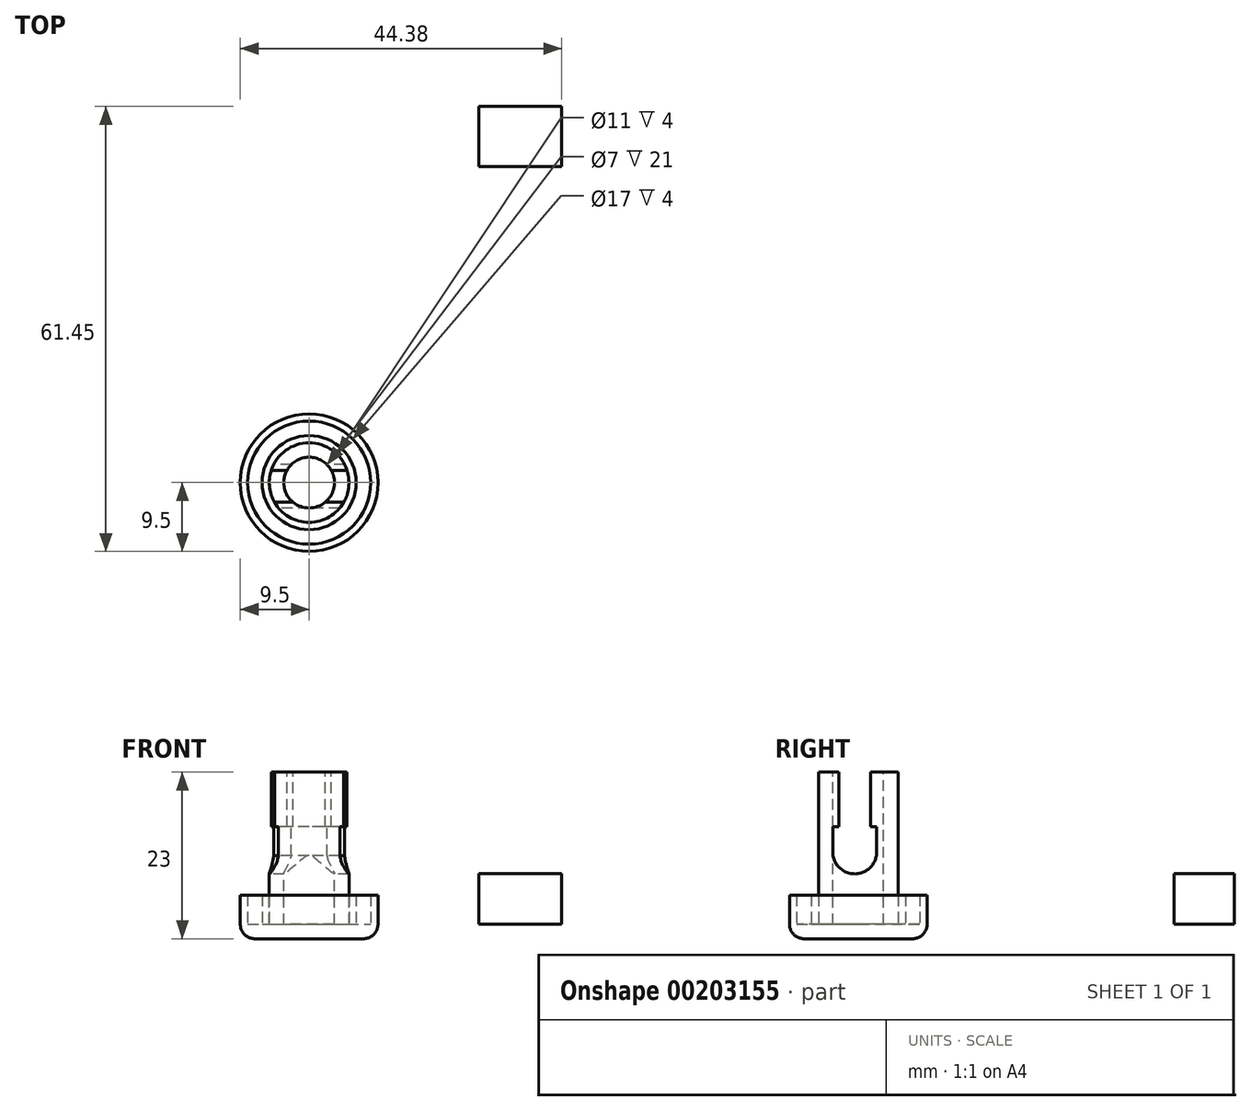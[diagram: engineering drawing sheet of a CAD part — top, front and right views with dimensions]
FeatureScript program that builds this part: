
annotation { "Feature Type Name" : "Feature", "Feature Type Description" : "" }
export const myFeature = defineFeature(function(context is Context, id is Id, definition is map)
    precondition{}
    {
        {
            var Q0;
            Q0=qCreatedBy(makeId("Top.planeOp"),FACE);
            var sketch = newSketch(context, id + "F0", { "sketchPlane" : qUnion([Q0])});
            skCircle(sketch, "E0", {"center": v(0, 0) * mm, "radius": 5.5 * mm});
            skCircle(sketch, "E1", {"center": v(0, 0) * mm, "radius": 8.5 * mm});
            skCircle(sketch, "E2", {"center": v(0, 0) * mm, "radius": 3.5 * mm});
            skSolve(sketch);
        }
        {
            var Q0;
            Q0=qCreatedBy(makeId("Top.planeOp"),FACE);
            var sketch = newSketch(context, id + "F1", { "sketchPlane" : qUnion([Q0])});
            skLineSegment(sketch, "E3.bottom", {"start": v(23.45, 51.95) * mm, "end": v(34.88, 51.95) * mm});
            skLineSegment(sketch, "E3.top", {"start": v(23.45, 43.64) * mm, "end": v(34.88, 43.64) * mm});
            skLineSegment(sketch, "E3.left", {"start": v(23.45, 51.95) * mm, "end": v(23.45, 43.64) * mm});
            skLineSegment(sketch, "E3.right", {"start": v(34.88, 51.95) * mm, "end": v(34.88, 43.64) * mm});
            skSolve(sketch);
        }
        {
            var Q0;
            Q0=makeQuery(id+"F1.imprint","IMPRINT",FACE,{"disambiguationData":[TD([[makeQuery(id+"F1.imprint","IMPRINT",EDGE,{"derivedFrom":sQuery(id+"F1.wireOp",EDGE,"E3.bottom")}),-1.0]])]});
            extrude(context, id + "F2", {"entities" : qUnion([Q0]), "oppositeDirection" : true, "depth" : 7 * mm});
        }
        {
            var Q0;
            Q0=qCreatedBy(makeId("Right.planeOp"),FACE);
            var sketch = newSketch(context, id + "F3", { "sketchPlane" : qUnion([Q0])});
            skLineSegment(sketch, "E4.top", {"start": v(-3.5, 17) * mm, "end": v(2.5, 17) * mm});
            skLineSegment(sketch, "E4.left", {"start": v(-3.5, 2.5) * mm, "end": v(-3.5, 6.5) * mm});
            skLineSegment(sketch, "E4.right", {"start": v(2.5, 2.5) * mm, "end": v(2.5, 6.5) * mm});
            skArc(sketch, "E5", {"start": v(-3.5, 2.5) * mm, "mid": v(-0.5, -0.04) * mm, "end": v(2.5, 2.5) * mm});
            skPoint(sketch, "E6.orphan", {"position": v(2.5, 0) * mm});
            skPoint(sketch, "E7.orphan", {"position": v(-3.5, 0) * mm});
            skPoint(sketch, "E8", {"position": v(-3.5, 6.5) * mm});
            skPoint(sketch, "E9", {"position": v(2.5, 6.5) * mm});
            skPoint(sketch, "E10", {"position": v(1.7, 17) * mm});
            skLineSegment(sketch, "E11", {"start": v(-2.7, 17) * mm, "end": v(-2.7, 6.5) * mm});
            skLineSegment(sketch, "E12", {"start": v(1.7, 17) * mm, "end": v(1.7, 6.5) * mm});
            skLineSegment(sketch, "E13", {"start": v(1.7, 6.5) * mm, "end": v(2.5, 6.5) * mm});
            skLineSegment(sketch, "E14", {"start": v(-2.7, 6.5) * mm, "end": v(-3.5, 6.5) * mm});
            skSolve(sketch);
        }
        {
            var Q0;
            Q0=makeQuery(id+"F2.opExtrude","CAP_FACE",FACE,{"disambiguationData":[OSD([sQuery(id+"F1.wireOp",EDGE,"E3.bottom"),sQuery(id+"F1.wireOp",EDGE,"E3.top"),sQuery(id+"F1.wireOp",EDGE,"E3.left"),sQuery(id+"F1.wireOp",EDGE,"E3.right")])],"isStart":false});
            var sketch = newSketch(context, id + "F4", { "sketchPlane" : qUnion([Q0])});
            skCircle(sketch, "E15", {"center": v(0, 0) * mm, "radius": 9.5 * mm});
            skCircle(sketch, "E16", {"center": v(0, 0) * mm, "radius": 5.5 * mm});
            skCircle(sketch, "E17", {"center": v(0, 0) * mm, "radius": 6.5 * mm});
            skSolve(sketch);
        }
        {
            var Q0;
            Q0=makeQuery(id+"F4.imprint","IMPRINT",FACE,{"disambiguationData":[TD([[makeQuery(id+"F4.imprint","IMPRINT",EDGE,{"derivedFrom":sQuery(id+"F4.wireOp",EDGE,"E15")}),1.0]])]});
            var Q1;
            Q1=makeQuery(id+"F4.imprint","IMPRINT",FACE,{"disambiguationData":[TD([[makeQuery(id+"F4.imprint","IMPRINT",EDGE,{"derivedFrom":sQuery(id+"F4.wireOp",EDGE,"E16")}),-1.0]])]});
            var Q2;
            Q2=makeQuery(id+"F4.imprint","IMPRINT",FACE,{"disambiguationData":[TD([[makeQuery(id+"F4.imprint","IMPRINT",EDGE,{"derivedFrom":sQuery(id+"F4.wireOp",EDGE,"E16")}),1.0]])]});
            extrude(context, id + "F5", {"entities" : qUnion([Q0, Q1, Q2]), "depth" : 2 * mm});
        }
        {
            var Q0;
            Q0=makeQuery(id+"F0.imprint","IMPRINT",FACE,{"disambiguationData":[TD([[makeQuery(id+"F0.imprint","IMPRINT",EDGE,{"derivedFrom":sQuery(id+"F0.wireOp",EDGE,"E0")}),1.0]])]});
            extrude(context, id + "F6", {"entities" : qUnion([Q0]), "operationType" : NewBodyOperationType.ADD, "oppositeDirection" : true, "depth" : 7 * mm});
        }
        {
            var Q0;
            Q0=makeQuery(id+"F6.opExtrude","CAP_FACE",FACE,{"disambiguationData":[OSD([sQuery(id+"F0.wireOp",EDGE,"E0"),sQuery(id+"F0.wireOp",EDGE,"E1")])],"isStart":true});
            extrude(context, id + "F7", {"entities" : qUnion([Q0]), "operationType" : NewBodyOperationType.ADD, "depth" : 14 * mm});
        }
        {
            var Q0;
            Q0=makeQuery(id+"F3.imprint","IMPRINT",FACE,{"disambiguationData":[TD([[makeQuery(id+"F3.imprint","IMPRINT",EDGE,{"derivedFrom":sQuery(id+"F3.wireOp",EDGE,"E4.left")}),-1.0]])]});
            extrude(context, id + "F8", {"entities" : qUnion([Q0]), "operationType" : NewBodyOperationType.REMOVE, "endBound" : BoundingType.SYMMETRIC, "depth" : 25 * mm});
        }
        {
            var Q0;
            Q0=makeQuery(id+"F5.opExtrude","CAP_EDGE",EDGE,{"disambiguationData":[OSD([sQuery(id+"F4.wireOp",EDGE,"E15")])],"isStart":false});
            fillet(context, id + "F9", {"entities" : qUnion([Q0]), "radius" : 2 * mm, "tangentPropagation" : true, "allowEdgeOverflow" : false});
        }
        {
            var Q0;
            Q0=makeQuery(id+"F4.imprint","IMPRINT",FACE,{"disambiguationData":[TD([[makeQuery(id+"F4.imprint","IMPRINT",EDGE,{"derivedFrom":makeQuery(id+"F2.opExtrude","CAP_EDGE",EDGE,{"disambiguationData":[OSD([sQuery(id+"F1.wireOp",EDGE,"E3.bottom")])],"isStart":false})}),1.0]])]});
            var sketch = newSketch(context, id + "F10", { "sketchPlane" : qUnion([Q0])});
            skCircle(sketch, "E18", {"center": v(0, 0) * mm, "radius": 8.5 * mm});
            skCircle(sketch, "E19", {"center": v(0, 0) * mm, "radius": 9.5 * mm});
            skSolve(sketch);
        }
        {
            var Q0;
            Q0=makeQuery(id+"F10.imprint","IMPRINT",FACE,{"disambiguationData":[TD([[makeQuery(id+"F10.imprint","IMPRINT",EDGE,{"derivedFrom":sQuery(id+"F10.wireOp",EDGE,"E18")}),-1.0]])]});
            extrude(context, id + "F11", {"entities" : qUnion([Q0]), "operationType" : NewBodyOperationType.ADD, "oppositeDirection" : true, "depth" : 4 * mm});
        }
        {
            var Q0;
            Q0=makeQuery(id+"F4.imprint","IMPRINT",FACE,{"disambiguationData":[TD([[makeQuery(id+"F4.imprint","IMPRINT",EDGE,{"derivedFrom":sQuery(id+"F4.wireOp",EDGE,"E16")}),-1.0]])]});
            extrude(context, id + "F12", {"entities" : qUnion([Q0]), "oppositeDirection" : true, "depth" : 4 * mm});
        }
    });
